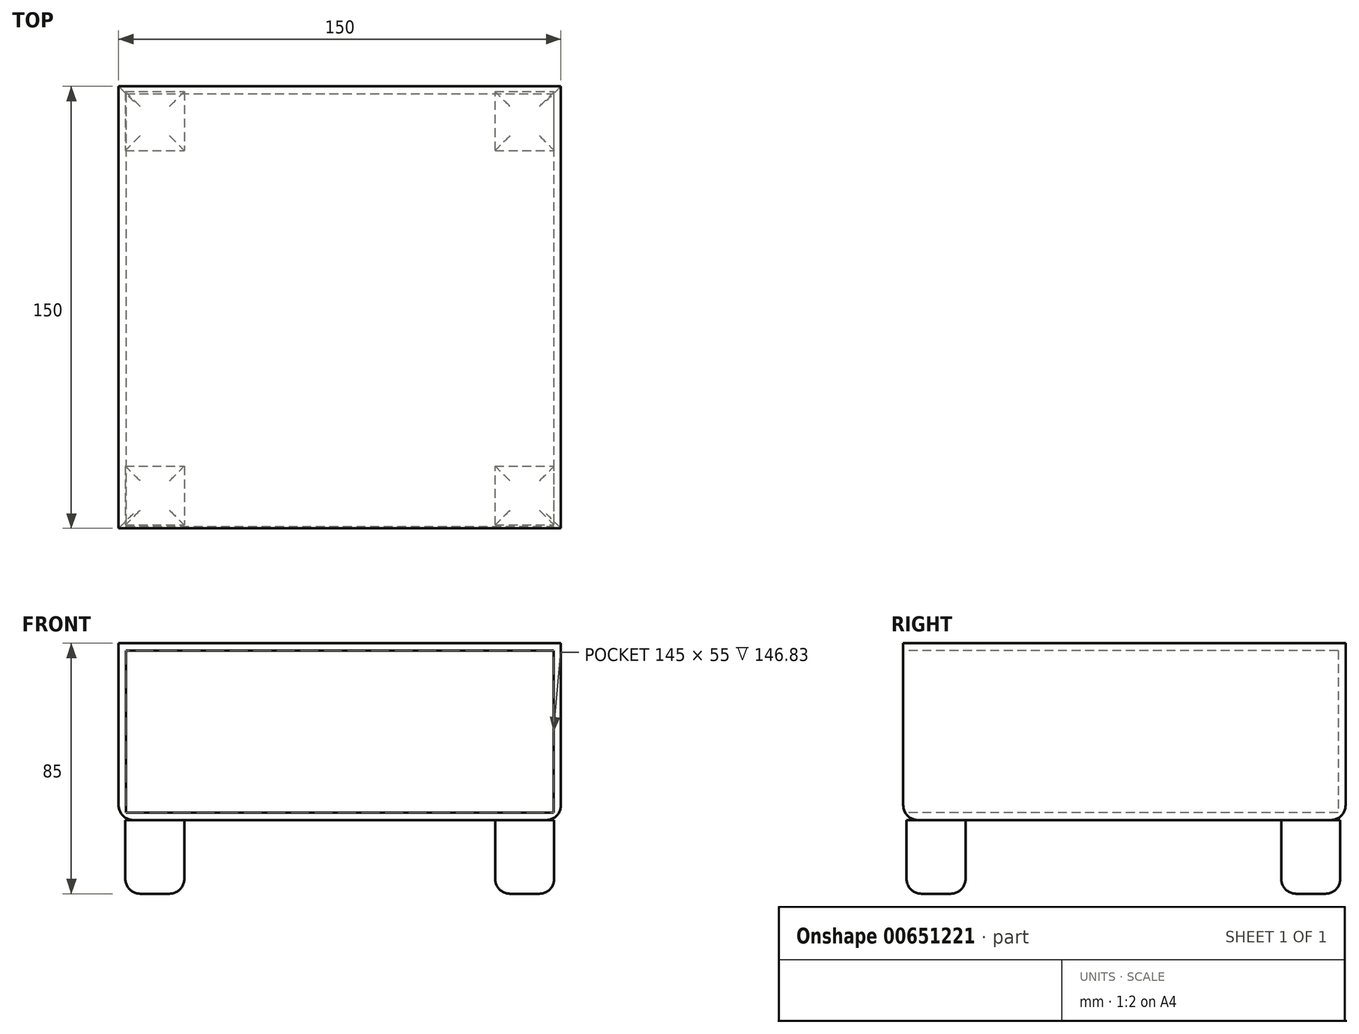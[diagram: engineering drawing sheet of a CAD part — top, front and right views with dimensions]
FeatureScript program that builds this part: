
annotation { "Feature Type Name" : "Feature", "Feature Type Description" : "" }
export const myFeature = defineFeature(function(context is Context, id is Id, definition is map)
    precondition{}
    {
        {
            var Q0;
            Q0=qCreatedBy(makeId("Top.planeOp"),FACE);
            var sketch = newSketch(context, id + "F0", { "sketchPlane" : qUnion([Q0])});
            skLineSegment(sketch, "E0.bottom", {"start": v(-72.72, 73.33) * mm, "end": v(-52.72, 73.33) * mm});
            skLineSegment(sketch, "E0.top", {"start": v(-72.72, 53.33) * mm, "end": v(-52.72, 53.33) * mm});
            skLineSegment(sketch, "E0.left", {"start": v(-72.72, 73.33) * mm, "end": v(-72.72, 53.33) * mm});
            skLineSegment(sketch, "E0.right", {"start": v(-52.72, 73.33) * mm, "end": v(-52.72, 53.33) * mm});
            skLineSegment(sketch, "E1.bottom", {"start": v(-72.72, -53.75) * mm, "end": v(-52.72, -53.75) * mm});
            skLineSegment(sketch, "E1.top", {"start": v(-72.72, -73.75) * mm, "end": v(-52.72, -73.75) * mm});
            skLineSegment(sketch, "E1.left", {"start": v(-72.72, -53.75) * mm, "end": v(-72.72, -73.75) * mm});
            skLineSegment(sketch, "E1.right", {"start": v(-52.72, -53.75) * mm, "end": v(-52.72, -73.75) * mm});
            skLineSegment(sketch, "E2.bottom", {"start": v(52.7, 53.33) * mm, "end": v(72.7, 53.33) * mm});
            skLineSegment(sketch, "E2.top", {"start": v(52.7, 73.33) * mm, "end": v(72.7, 73.33) * mm});
            skLineSegment(sketch, "E2.left", {"start": v(52.7, 53.33) * mm, "end": v(52.7, 73.33) * mm});
            skLineSegment(sketch, "E2.right", {"start": v(72.7, 53.33) * mm, "end": v(72.7, 73.33) * mm});
            skLineSegment(sketch, "E3.bottom", {"start": v(52.7, -73.75) * mm, "end": v(72.7, -73.75) * mm});
            skLineSegment(sketch, "E3.top", {"start": v(52.7, -53.75) * mm, "end": v(72.7, -53.75) * mm});
            skLineSegment(sketch, "E3.left", {"start": v(52.7, -73.75) * mm, "end": v(52.7, -53.75) * mm});
            skLineSegment(sketch, "E3.right", {"start": v(72.7, -73.75) * mm, "end": v(72.7, -53.75) * mm});
            skSolve(sketch);
        }
        {
            var Q0;
            Q0=makeQuery(id+"F0.imprint","IMPRINT",FACE,{"disambiguationData":[TD([[makeQuery(id+"F0.imprint","IMPRINT",EDGE,{"derivedFrom":sQuery(id+"F0.wireOp",EDGE,"E0.bottom")}),-1.0]])]});
            var Q1;
            Q1=makeQuery(id+"F0.imprint","IMPRINT",FACE,{"disambiguationData":[TD([[makeQuery(id+"F0.imprint","IMPRINT",EDGE,{"derivedFrom":sQuery(id+"F0.wireOp",EDGE,"E1.bottom")}),-1.0]])]});
            var Q2;
            Q2=makeQuery(id+"F0.imprint","IMPRINT",FACE,{"disambiguationData":[TD([[makeQuery(id+"F0.imprint","IMPRINT",EDGE,{"derivedFrom":sQuery(id+"F0.wireOp",EDGE,"E2.bottom")}),1.0]])]});
            var Q3;
            Q3=makeQuery(id+"F0.imprint","IMPRINT",FACE,{"disambiguationData":[TD([[makeQuery(id+"F0.imprint","IMPRINT",EDGE,{"derivedFrom":sQuery(id+"F0.wireOp",EDGE,"E3.bottom")}),1.0]])]});
            extrude(context, id + "F1", {"entities" : qUnion([Q0, Q1, Q2, Q3]), "oppositeDirection" : true, "depth" : 25 * mm, "offsetDistance" : 25 * mm});
        }
        {
            var Q0;
            Q0=qCreatedBy(makeId("Top.planeOp"),FACE);
            var sketch = newSketch(context, id + "F2", { "sketchPlane" : qUnion([Q0])});
            skLineSegment(sketch, "E4.bottom", {"start": v(-75, 75.13) * mm, "end": v(75, 75.13) * mm});
            skLineSegment(sketch, "E4.top", {"start": v(-75, -74.87) * mm, "end": v(75, -74.87) * mm});
            skLineSegment(sketch, "E4.left", {"start": v(-75, 75.13) * mm, "end": v(-75, -74.87) * mm});
            skLineSegment(sketch, "E4.right", {"start": v(75, 75.13) * mm, "end": v(75, -74.87) * mm});
            skSolve(sketch);
        }
        {
            var Q0;
            Q0 = qSketchRegion(id + "F2", true);
            extrude(context, id + "F3", {"entities" : qUnion([Q0]), "depth" : 60 * mm, "offsetDistance" : 25 * mm});
        }
        {
            var Q0;
            Q0=makeQuery(id+"F3.opExtrude","SWEPT_FACE",FACE,{"disambiguationData":[OSD([sQuery(id+"F2.wireOp",EDGE,"E4.top")])]});
            shell(context, id + "F4", {"entities" : qUnion([Q0]), "thickness" : 2.5 * mm});
        }
        {
            var Q0;
            Q0=makeQuery(id+"F1.opExtrude","CAP_FACE",FACE,{"disambiguationData":[OSD([sQuery(id+"F0.wireOp",EDGE,"E1.bottom"),sQuery(id+"F0.wireOp",EDGE,"E1.top"),sQuery(id+"F0.wireOp",EDGE,"E1.left"),sQuery(id+"F0.wireOp",EDGE,"E1.right")])],"isStart":false});
            var Q1;
            Q1=makeQuery(id+"F1.opExtrude","CAP_FACE",FACE,{"disambiguationData":[OSD([sQuery(id+"F0.wireOp",EDGE,"E3.bottom"),sQuery(id+"F0.wireOp",EDGE,"E3.top"),sQuery(id+"F0.wireOp",EDGE,"E3.left"),sQuery(id+"F0.wireOp",EDGE,"E3.right")])],"isStart":false});
            var Q2;
            Q2=makeQuery(id+"F1.opExtrude","CAP_FACE",FACE,{"disambiguationData":[OSD([sQuery(id+"F0.wireOp",EDGE,"E2.bottom"),sQuery(id+"F0.wireOp",EDGE,"E2.top"),sQuery(id+"F0.wireOp",EDGE,"E2.left"),sQuery(id+"F0.wireOp",EDGE,"E2.right")])],"isStart":false});
            var Q3;
            Q3=makeQuery(id+"F1.opExtrude","CAP_FACE",FACE,{"disambiguationData":[OSD([sQuery(id+"F0.wireOp",EDGE,"E0.bottom"),sQuery(id+"F0.wireOp",EDGE,"E0.top"),sQuery(id+"F0.wireOp",EDGE,"E0.left"),sQuery(id+"F0.wireOp",EDGE,"E0.right")])],"isStart":false});
            fillet(context, id + "F5", {"entities" : qUnion([Q0, Q1, Q2, Q3]), "radius" : 5 * mm, "tangentPropagation" : true, "allowEdgeOverflow" : false});
        }
        {
            var Q0;
            Q0=makeQuery(id+"F3.opExtrude","CAP_FACE",FACE,{"disambiguationData":[OSD([sQuery(id+"F2.wireOp",EDGE,"E4.bottom"),sQuery(id+"F2.wireOp",EDGE,"E4.top"),sQuery(id+"F2.wireOp",EDGE,"E4.left"),sQuery(id+"F2.wireOp",EDGE,"E4.right")])],"isStart":true});
            fillet(context, id + "F6", {"entities" : qUnion([Q0]), "radius" : 5 * mm, "tangentPropagation" : true, "allowEdgeOverflow" : false});
        }
    });
